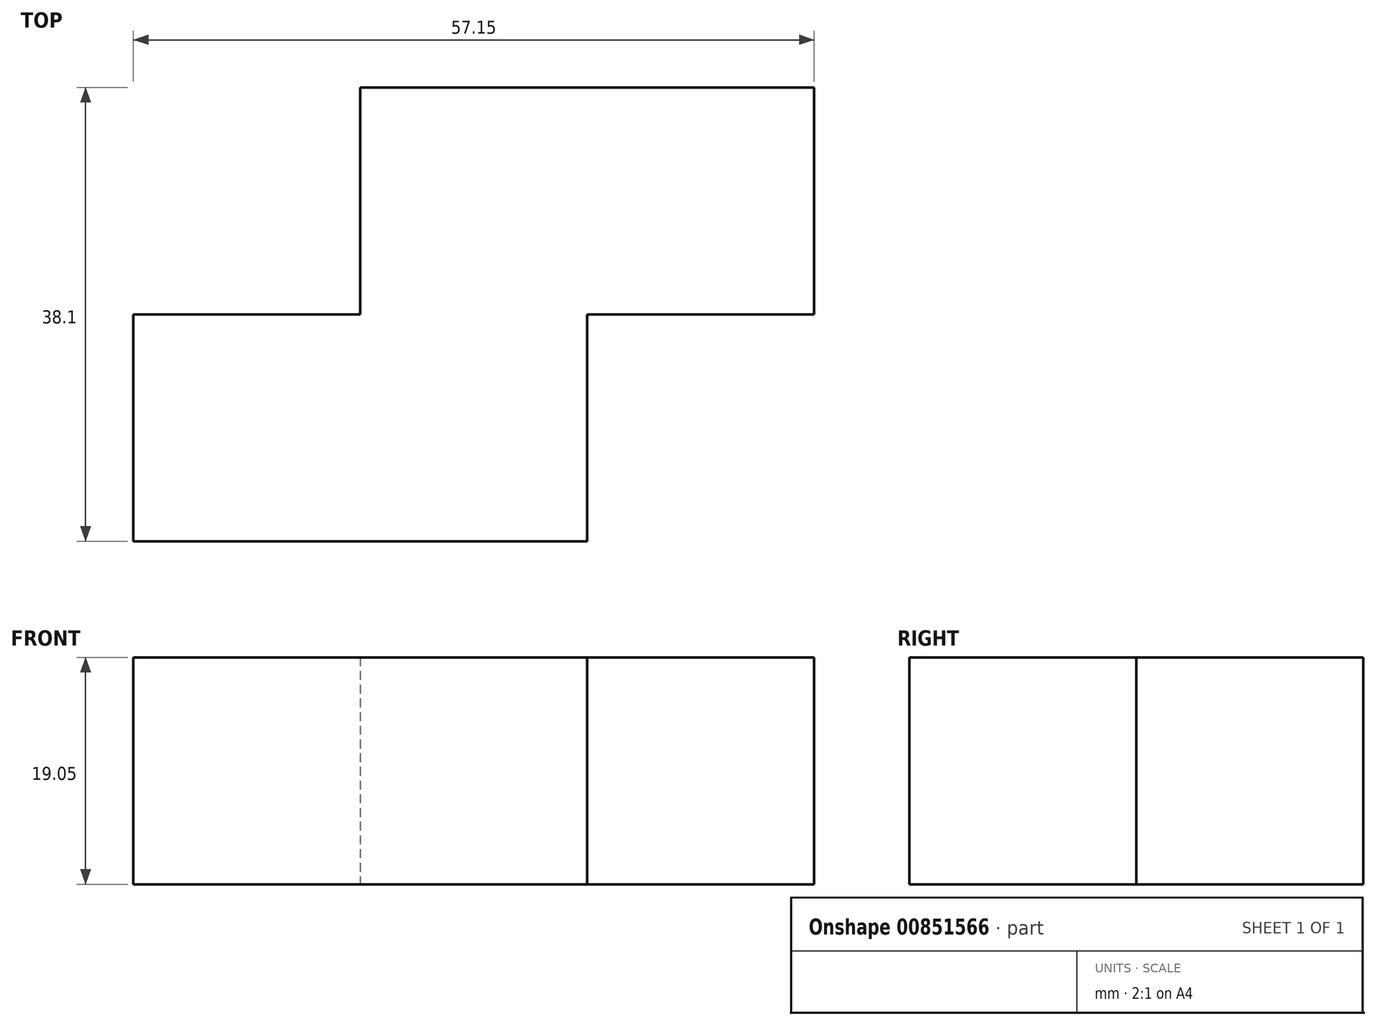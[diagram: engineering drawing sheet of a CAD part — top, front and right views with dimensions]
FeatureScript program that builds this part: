
annotation { "Feature Type Name" : "Feature", "Feature Type Description" : "" }
export const myFeature = defineFeature(function(context is Context, id is Id, definition is map)
    precondition{}
    {
        {
            var Q0;
            Q0=qCreatedBy(makeId("Top.planeOp"),FACE);
            var sketch = newSketch(context, id + "F0", { "sketchPlane" : qUnion([Q0])});
            skLineSegment(sketch, "E0.bottom", {"start": v(0, 0) * mm, "end": v(19.05, 0) * mm});
            skLineSegment(sketch, "E0.top", {"start": v(0, 19.05) * mm, "end": v(19.05, 19.05) * mm});
            skLineSegment(sketch, "E0.left", {"start": v(0, 0) * mm, "end": v(0, 19.05) * mm});
            skLineSegment(sketch, "E0.right", {"start": v(19.05, 0) * mm, "end": v(19.05, 19.05) * mm});
            skLineSegment(sketch, "E1.MirrorCS", {"start": v(0, 38.1) * mm, "end": v(19.05, 38.1) * mm});
            skLineSegment(sketch, "E2.MirrorCS", {"start": v(0, 38.1) * mm, "end": v(0, 19.05) * mm});
            skLineSegment(sketch, "E3.MirrorCS", {"start": v(19.05, 38.1) * mm, "end": v(19.05, 19.05) * mm});
            skLineSegment(sketch, "E4.MirrorCS", {"start": v(-19.05, 0) * mm, "end": v(-19.05, 19.05) * mm});
            skLineSegment(sketch, "E5.MirrorCS", {"start": v(0, 19.05) * mm, "end": v(-19.05, 19.05) * mm});
            skLineSegment(sketch, "E6.MirrorCS", {"start": v(0, 0) * mm, "end": v(-19.05, 0) * mm});
            skLineSegment(sketch, "E7.MirrorCS", {"start": v(38.1, 38.1) * mm, "end": v(38.1, 19.05) * mm});
            skLineSegment(sketch, "E8.MirrorCS", {"start": v(38.1, 38.1) * mm, "end": v(19.05, 38.1) * mm});
            skLineSegment(sketch, "E9.MirrorCS", {"start": v(38.1, 19.05) * mm, "end": v(19.05, 19.05) * mm});
            skSolve(sketch);
        }
        {
            var Q0;
            Q0=makeQuery(id+"F0.imprint","IMPRINT",FACE,{"disambiguationData":[TD([[makeQuery(id+"F0.imprint","IMPRINT",EDGE,{"derivedFrom":sQuery(id+"F0.wireOp",EDGE,"E0.left")}),1.0]])]});
            var Q1;
            Q1=makeQuery(id+"F0.imprint","IMPRINT",FACE,{"disambiguationData":[TD([[makeQuery(id+"F0.imprint","IMPRINT",EDGE,{"derivedFrom":sQuery(id+"F0.wireOp",EDGE,"E3.MirrorCS")}),1.0]])]});
            var Q2;
            Q2=makeQuery(id+"F0.imprint","IMPRINT",FACE,{"disambiguationData":[TD([[makeQuery(id+"F0.imprint","IMPRINT",EDGE,{"derivedFrom":sQuery(id+"F0.wireOp",EDGE,"E0.bottom")}),1.0]])]});
            var Q3;
            Q3=makeQuery(id+"F0.imprint","IMPRINT",FACE,{"disambiguationData":[TD([[makeQuery(id+"F0.imprint","IMPRINT",EDGE,{"derivedFrom":sQuery(id+"F0.wireOp",EDGE,"E0.top")}),1.0]])]});
            extrude(context, id + "F1", {"entities" : qUnion([Q0, Q1, Q2, Q3]), "depth" : 19.05 * mm, "offsetDistance" : 25.4 * mm});
        }
    });
